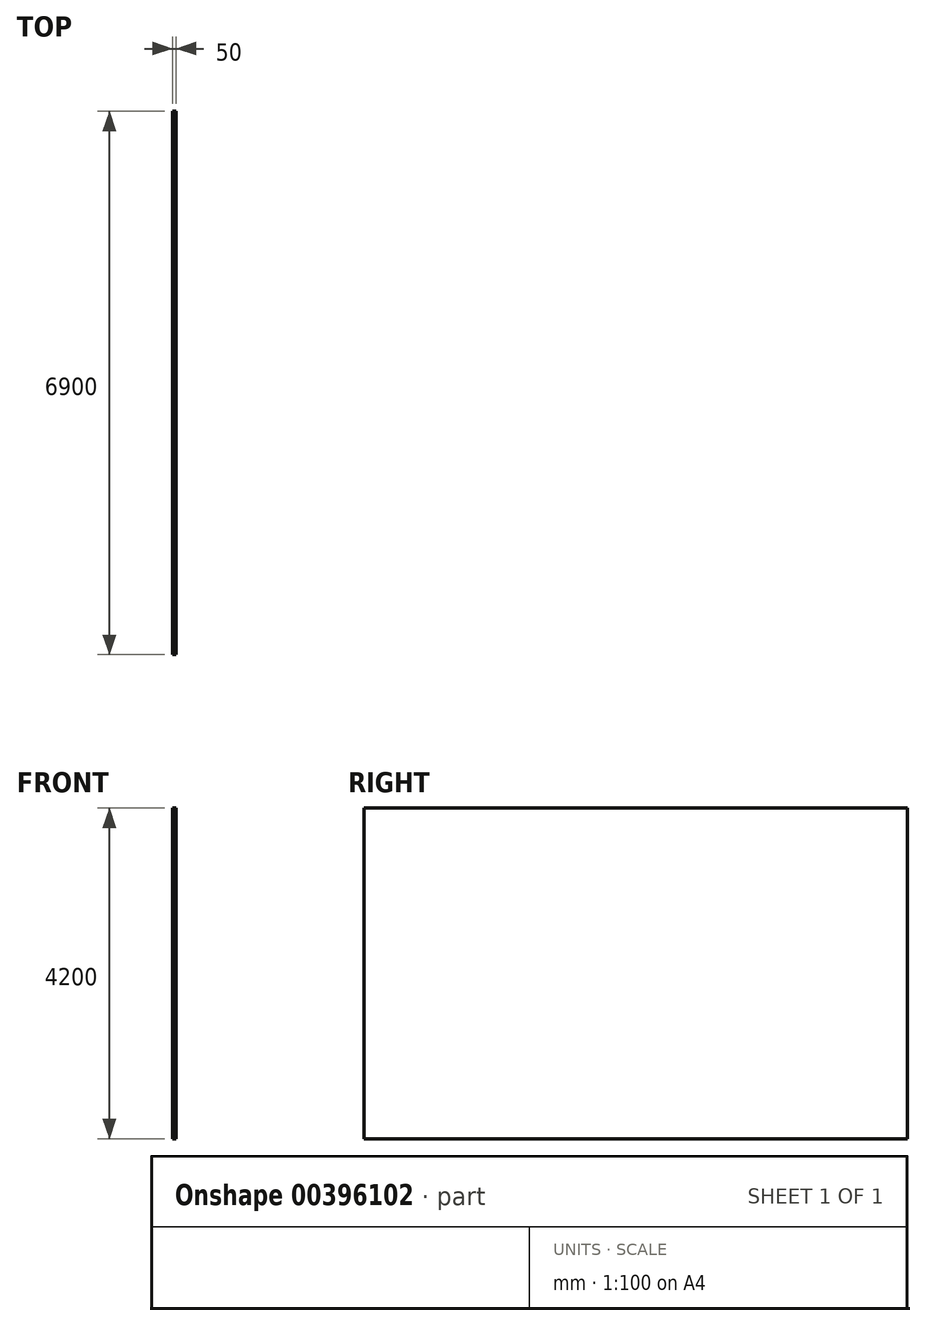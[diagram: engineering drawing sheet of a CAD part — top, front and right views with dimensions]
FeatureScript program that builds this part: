
annotation { "Feature Type Name" : "Feature", "Feature Type Description" : "" }
export const myFeature = defineFeature(function(context is Context, id is Id, definition is map)
    precondition{}
    {
        {
            var Q0;
            Q0=qCreatedBy(makeId("Top.planeOp"),FACE);
            var sketch = newSketch(context, id + "F0", { "sketchPlane" : qUnion([Q0])});
            skLineSegment(sketch, "E0.bottom", {"start": v(0, 0) * mm, "end": v(50, 0) * mm});
            skLineSegment(sketch, "E0.top", {"start": v(0, 6900) * mm, "end": v(50, 6900) * mm});
            skLineSegment(sketch, "E0.left", {"start": v(0, 0) * mm, "end": v(0, 6900) * mm});
            skLineSegment(sketch, "E0.right", {"start": v(50, 0) * mm, "end": v(50, 6900) * mm});
            skSolve(sketch);
        }
        {
            var Q0;
            Q0=makeQuery(id+"F0.imprint","IMPRINT",FACE,{"disambiguationData":[TD([[makeQuery(id+"F0.imprint","IMPRINT",EDGE,{"derivedFrom":sQuery(id+"F0.wireOp",EDGE,"E0.bottom")}),1.0]])]});
            extrude(context, id + "F1", {"entities" : qUnion([Q0]), "depth" : 4200 * mm});
        }
    });
